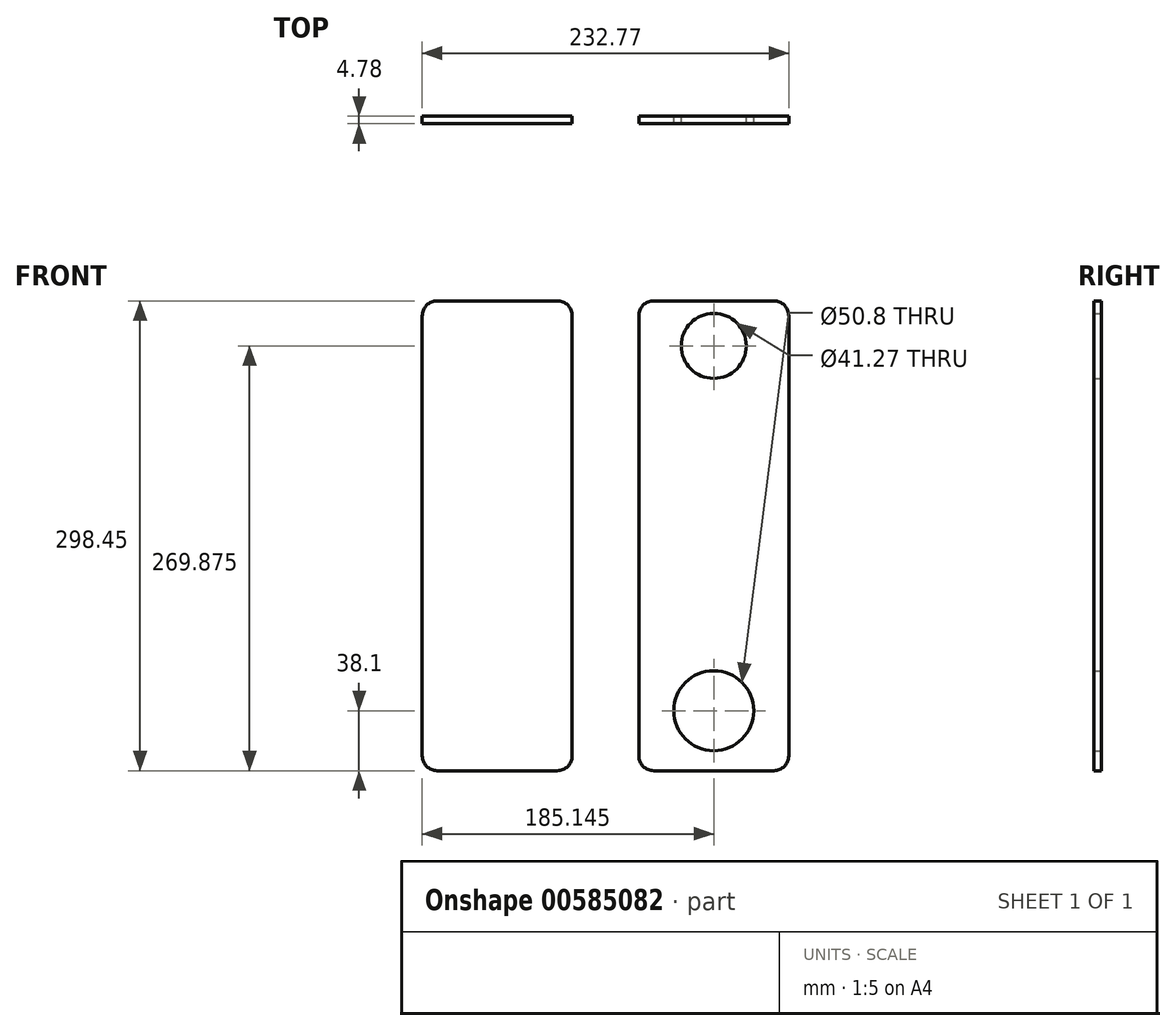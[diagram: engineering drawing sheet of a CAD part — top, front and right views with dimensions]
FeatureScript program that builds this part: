
annotation { "Feature Type Name" : "Feature", "Feature Type Description" : "" }
export const myFeature = defineFeature(function(context is Context, id is Id, definition is map)
    precondition{}
    {
        {
            var Q0;
            Q0=qCreatedBy(makeId("Front.planeOp"),FACE);
            var sketch = newSketch(context, id + "F0", { "sketchPlane" : qUnion([Q0])});
            skLineSegment(sketch, "E0.bottom", {"start": v(0, 0) * mm, "end": v(95.25, 0) * mm});
            skLineSegment(sketch, "E0.top", {"start": v(0, 298.45) * mm, "end": v(95.25, 298.45) * mm});
            skLineSegment(sketch, "E0.left", {"start": v(0, 0) * mm, "end": v(0, 298.45) * mm});
            skLineSegment(sketch, "E0.right", {"start": v(95.25, 0) * mm, "end": v(95.25, 298.45) * mm});
            skCircle(sketch, "E1", {"center": v(47.62, 38.1) * mm, "radius": 25.4 * mm});
            skCircle(sketch, "E2", {"center": v(47.62, 269.88) * mm, "radius": 20.64 * mm});
            skSolve(sketch);
        }
        {
            var Q0;
            Q0=makeQuery(id+"F0.imprint","IMPRINT",FACE,{"disambiguationData":[TD([[makeQuery(id+"F0.imprint","IMPRINT",EDGE,{"derivedFrom":sQuery(id+"F0.wireOp",EDGE,"E0.bottom")}),1.0]])]});
            extrude(context, id + "F1", {"entities" : qUnion([Q0]), "depth" : 4.78 * mm, "offsetDistance" : 25.4 * mm});
        }
        {
            var Q0;
            Q0=makeQuery(id+"F1.opExtrude","SWEPT_EDGE",EDGE,{"disambiguationData":[OSD([sQuery(id+"F0.wireOp",EDGE,"E0.top"),sQuery(id+"F0.wireOp",EDGE,"E0.left")])]});
            var Q1;
            Q1=makeQuery(id+"F1.opExtrude","SWEPT_EDGE",EDGE,{"disambiguationData":[OSD([sQuery(id+"F0.wireOp",EDGE,"E0.top"),sQuery(id+"F0.wireOp",EDGE,"E0.right")])]});
            var Q2;
            Q2=makeQuery(id+"F1.opExtrude","SWEPT_EDGE",EDGE,{"disambiguationData":[OSD([sQuery(id+"F0.wireOp",EDGE,"E0.bottom"),sQuery(id+"F0.wireOp",EDGE,"E0.left")])]});
            var Q3;
            Q3=makeQuery(id+"F1.opExtrude","SWEPT_EDGE",EDGE,{"disambiguationData":[OSD([sQuery(id+"F0.wireOp",EDGE,"E0.bottom"),sQuery(id+"F0.wireOp",EDGE,"E0.right")])]});
            fillet(context, id + "F2", {"entities" : qUnion([Q0, Q1, Q2, Q3]), "radius" : 9.52 * mm, "tangentPropagation" : true, "defaultsChanged" : true, "vertexSettings" : [], "allowEdgeOverflow" : false});
        }
        {
            var Q0;
            Q0=qCreatedBy(makeId("Front.planeOp"),FACE);
            var sketch = newSketch(context, id + "F3", { "sketchPlane" : qUnion([Q0])});
            skLineSegment(sketch, "E3.bottom", {"start": v(-137.52, 0) * mm, "end": v(-42.27, 0) * mm});
            skLineSegment(sketch, "E3.top", {"start": v(-137.52, 298.45) * mm, "end": v(-42.27, 298.45) * mm});
            skLineSegment(sketch, "E3.left", {"start": v(-137.52, 0) * mm, "end": v(-137.52, 298.45) * mm});
            skLineSegment(sketch, "E3.right", {"start": v(-42.27, 0) * mm, "end": v(-42.27, 298.45) * mm});
            skSolve(sketch);
        }
        {
            var Q0;
            Q0 = qSketchRegion(id + "F3", true);
            extrude(context, id + "F4", {"entities" : qUnion([Q0]), "depth" : 4.78 * mm, "offsetDistance" : 25.4 * mm});
        }
        {
            var Q0;
            Q0=makeQuery(id+"F4.opExtrude","SWEPT_EDGE",EDGE,{"disambiguationData":[OSD([sQuery(id+"F3.wireOp",EDGE,"E3.top"),sQuery(id+"F3.wireOp",EDGE,"E3.left")])]});
            var Q1;
            Q1=makeQuery(id+"F4.opExtrude","SWEPT_EDGE",EDGE,{"disambiguationData":[OSD([sQuery(id+"F3.wireOp",EDGE,"E3.top"),sQuery(id+"F3.wireOp",EDGE,"E3.right")])]});
            var Q2;
            Q2=makeQuery(id+"F4.opExtrude","SWEPT_EDGE",EDGE,{"disambiguationData":[OSD([sQuery(id+"F3.wireOp",EDGE,"E3.bottom"),sQuery(id+"F3.wireOp",EDGE,"E3.right")])]});
            var Q3;
            Q3=makeQuery(id+"F4.opExtrude","SWEPT_EDGE",EDGE,{"disambiguationData":[OSD([sQuery(id+"F3.wireOp",EDGE,"E3.bottom"),sQuery(id+"F3.wireOp",EDGE,"E3.left")])]});
            fillet(context, id + "F5", {"entities" : qUnion([Q0, Q1, Q2, Q3]), "tangentPropagation" : true, "radius" : 9.52 * mm, "defaultsChanged" : true, "vertexSettings" : [], "allowEdgeOverflow" : false});
        }
    });
